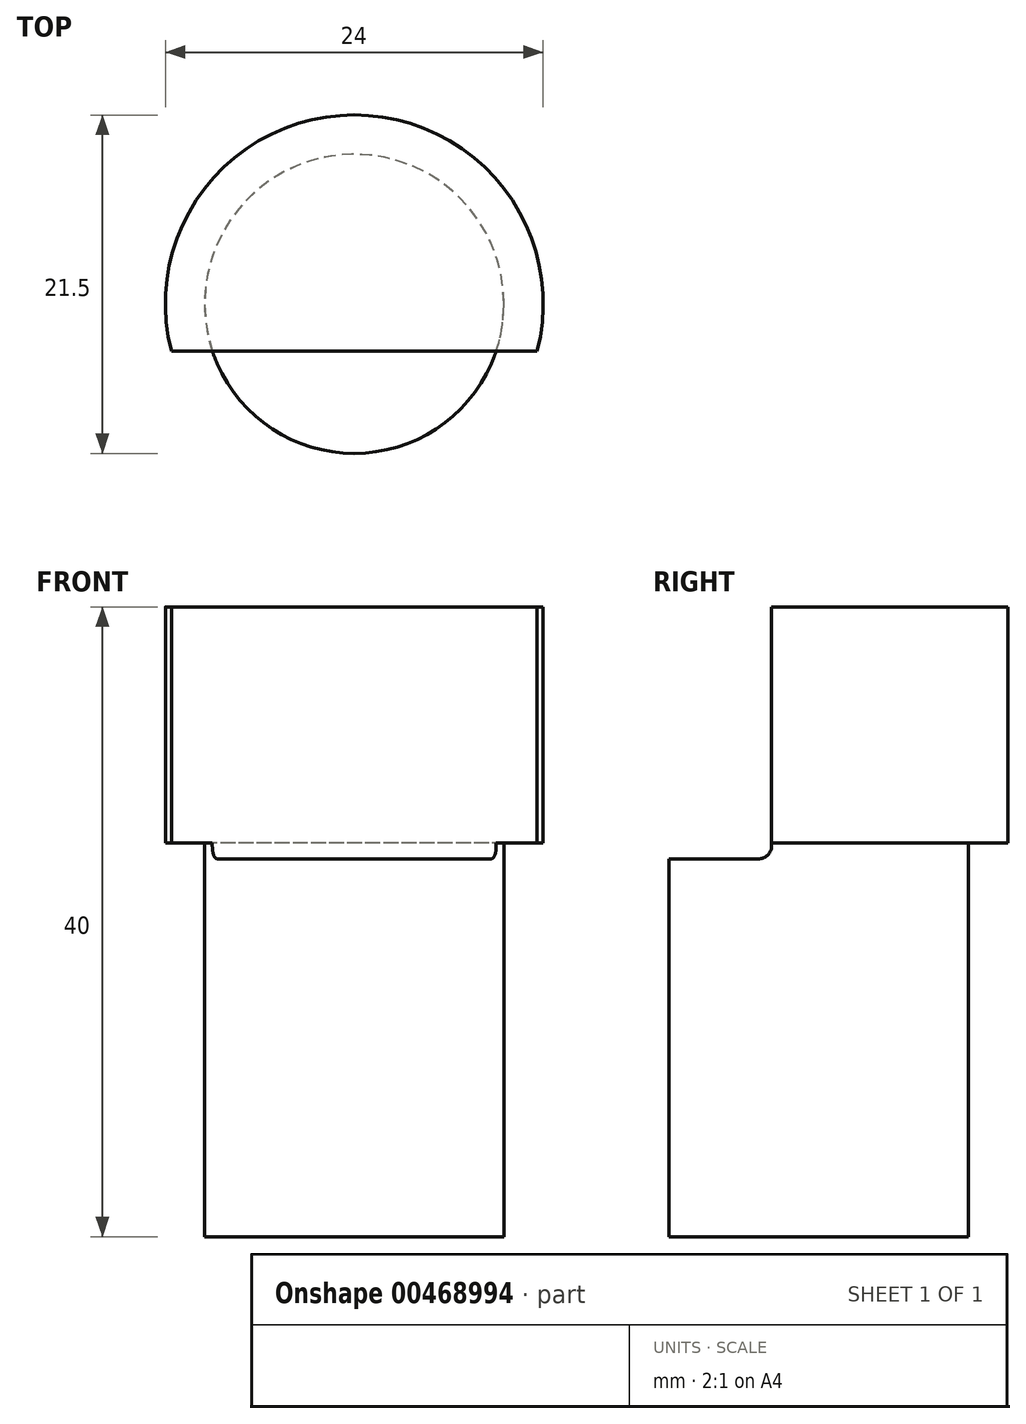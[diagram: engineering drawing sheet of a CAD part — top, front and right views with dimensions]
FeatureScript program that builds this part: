
annotation { "Feature Type Name" : "Feature", "Feature Type Description" : "" }
export const myFeature = defineFeature(function(context is Context, id is Id, definition is map)
    precondition{}
    {
        {
            var Q0;
            Q0=qCreatedBy(makeId("Top.planeOp"),FACE);
            var sketch = newSketch(context, id + "F0", { "sketchPlane" : qUnion([Q0])});
            skCircle(sketch, "E0", {"center": v(0, 0) * mm, "radius": 9.5 * mm});
            skSolve(sketch);
        }
        {
            var Q0;
            Q0=makeQuery(id+"F0.imprint","IMPRINT",FACE,{"disambiguationData":[TD([[makeQuery(id+"F0.imprint","IMPRINT",EDGE,{"derivedFrom":sQuery(id+"F0.wireOp",EDGE,"E0")}),1.0]])]});
            extrude(context, id + "F1", {"entities" : qUnion([Q0]), "oppositeDirection" : true, "depth" : 25 * mm});
        }
        {
            var Q0;
            Q0=makeQuery(id+"F1.opExtrude","CAP_FACE",FACE,{"disambiguationData":[OSD([sQuery(id+"F0.wireOp",EDGE,"E0")])],"isStart":true});
            var sketch = newSketch(context, id + "F2", { "sketchPlane" : qUnion([Q0])});
            skCircle(sketch, "E1", {"center": v(0, 0) * mm, "radius": 12 * mm});
            skSolve(sketch);
        }
        {
            var Q0;
            Q0=makeQuery(id+"F2.imprint","IMPRINT",FACE,{"disambiguationData":[TD([[makeQuery(id+"F2.imprint","IMPRINT",EDGE,{"derivedFrom":sQuery(id+"F2.wireOp",EDGE,"E1")}),1.0]])]});
            var Q1;
            Q1=makeQuery(id+"F2.imprint","IMPRINT",FACE,{"disambiguationData":[TD([[makeQuery(id+"F2.imprint","IMPRINT",EDGE,{"derivedFrom":makeQuery(id+"F1.opExtrude","CAP_EDGE",EDGE,{"disambiguationData":[OSD([sQuery(id+"F0.wireOp",EDGE,"E0")])],"isStart":true})}),1.0]])]});
            extrude(context, id + "F3", {"entities" : qUnion([Q0, Q1]), "operationType" : NewBodyOperationType.ADD, "depth" : 15 * mm});
        }
        {
            var Q0;
            Q0=qCreatedBy(makeId("Top.planeOp"),FACE);
            cPlane(context, id + "F4", {"entities" : qUnion([Q0]), "cplaneType" : CPlaneType.OFFSET, "offset" : 1 * mm, "oppositeDirection" : true, "width" : 150 * mm, "height" : 150 * mm});
        }
        {
            var Q0;
            Q0=qCreatedBy(makeId("Front.planeOp"),FACE);
            cPlane(context, id + "F5", {"entities" : qUnion([Q0]), "cplaneType" : CPlaneType.OFFSET, "offset" : 3 * mm, "width" : 150 * mm, "height" : 150 * mm});
        }
        {
            var Q0;
            Q0=qCreatedBy(makeId("Right.planeOp"),FACE);
            var sketch = newSketch(context, id + "F6", { "sketchPlane" : qUnion([Q0])});
            skLineSegment(sketch, "E2", {"start": v(-3, -12.3) * mm, "end": v(-3, 42.01) * mm});
            skLineSegment(sketch, "E3", {"start": v(-27.48, -1) * mm, "end": v(26.82, -1) * mm});
            skLineSegment(sketch, "E4", {"start": v(12, 15) * mm, "end": v(12, 0) * mm});
            skLineSegment(sketch, "E5", {"start": v(-12, 0) * mm, "end": v(-12, 15) * mm});
            skLineSegment(sketch, "E6", {"start": v(12, 15) * mm, "end": v(-12, 15) * mm});
            skLineSegment(sketch, "E7", {"start": v(-9.5, 0) * mm, "end": v(-12, 0) * mm});
            skLineSegment(sketch, "E8", {"start": v(12, 0) * mm, "end": v(9.5, 0) * mm});
            skLineSegment(sketch, "E9", {"start": v(-9.5, 0) * mm, "end": v(-9.5, -25) * mm});
            skLineSegment(sketch, "E10", {"start": v(9.5, -25) * mm, "end": v(9.5, 0) * mm});
            skSolve(sketch);
        }
        {
            var Q0;
            {var subQ0=sQuery(id+"F6.wireOp",EDGE,"E5");Q0=makeQuery(id+"F6.imprint","IMPRINT",FACE,{"disambiguationData":[TD([[makeQuery(id+"F6.imprint","IMPRINT",EDGE,{"derivedFrom":subQ0}),-1.0]])]});}
            extrude(context, id + "F7", {"entities" : qUnion([Q0]), "operationType" : NewBodyOperationType.REMOVE, "endBound" : BoundingType.SYMMETRIC, "depth" : 25 * mm});
        }
        {
            var Q0;
            Q0=makeQuery(id+"F7.boolean.opBoolean","COPY",EDGE,{"derivedFrom":makeQuery(id+"F7.opExtrude","SWEPT_EDGE",EDGE,{"disambiguationData":[OSD([sQuery(id+"F6.wireOp",EDGE,"E2"),sQuery(id+"F6.wireOp",EDGE,"E3")])]})});
            fillet(context, id + "F8", {"entities" : qUnion([Q0]), "radius" : .8 * mm, "tangentPropagation" : true, "allowEdgeOverflow" : false});
        }
    });
